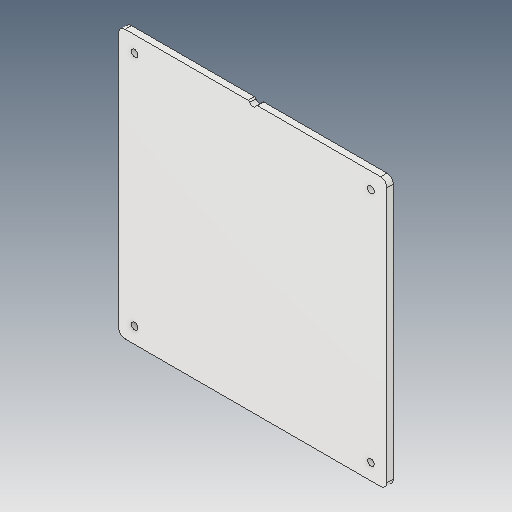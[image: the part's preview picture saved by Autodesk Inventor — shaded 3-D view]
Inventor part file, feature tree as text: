
AUTODESK INVENTOR PART (.ipt)
format: ipt  version: 2023.5 (Build 275446000, 446)  size: 97,280 bytes
history: native  units: in
note: dims shown in document units (in); Inventor stores cm internally (conversion verified against a paired STEP export)
features: fillet x1
ambient origin geometry x8: Origin, YZ Plane, XZ Plane, XY Plane, X Axis, Y Axis, Z Axis, Center Point
bodies: Solid1 (feature_tree)
feature tree (1):
  fillet  "Fillet2"  [1 undecoded]
note: 1 required parameter value undecoded (feature->parameter linkage not recoverable at this tier; creation-order binding heuristic only, values carry confidence <= 0.55)
